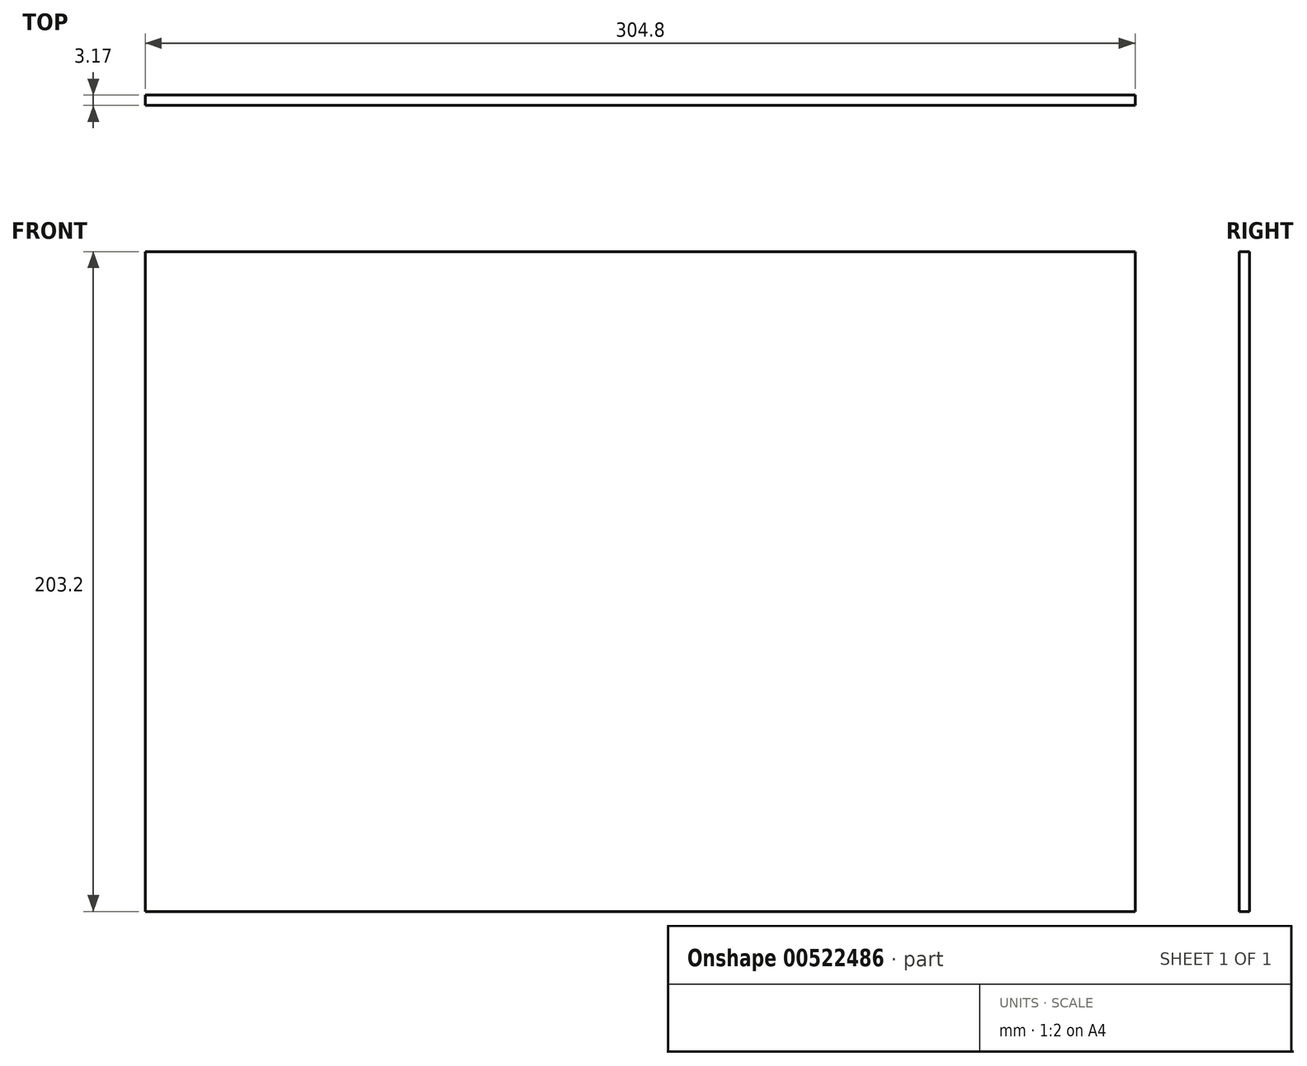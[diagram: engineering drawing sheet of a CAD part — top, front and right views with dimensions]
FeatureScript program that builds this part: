
annotation { "Feature Type Name" : "Feature", "Feature Type Description" : "" }
export const myFeature = defineFeature(function(context is Context, id is Id, definition is map)
    precondition{}
    {
        {
            var Q0;
            Q0=qCreatedBy(makeId("Front.planeOp"),FACE);
            var sketch = newSketch(context, id + "F0", { "sketchPlane" : qUnion([Q0])});
            skLineSegment(sketch, "E0.bottom", {"start": v(152.4, 101.6) * mm, "end": v(-152.4, 101.6) * mm});
            skLineSegment(sketch, "E0.top", {"start": v(152.4, -101.6) * mm, "end": v(-152.4, -101.6) * mm});
            skLineSegment(sketch, "E0.left", {"start": v(152.4, 101.6) * mm, "end": v(152.4, -101.6) * mm});
            skLineSegment(sketch, "E0.right", {"start": v(-152.4, 101.6) * mm, "end": v(-152.4, -101.6) * mm});
            skPoint(sketch, "E0.middle", {"position": v(0, 0) * mm});
            skSolve(sketch);
        }
        {
            var Q0;
            Q0=makeQuery(id+"F0.imprint","IMPRINT",FACE,{"disambiguationData":[TD([[makeQuery(id+"F0.imprint","IMPRINT",EDGE,{"derivedFrom":sQuery(id+"F0.wireOp",EDGE,"E0.bottom")}),1.0]])]});
            extrude(context, id + "F1", {"entities" : qUnion([Q0]), "depth" : 3.17 * mm, "offsetDistance" : 25.4 * mm});
        }
    });
